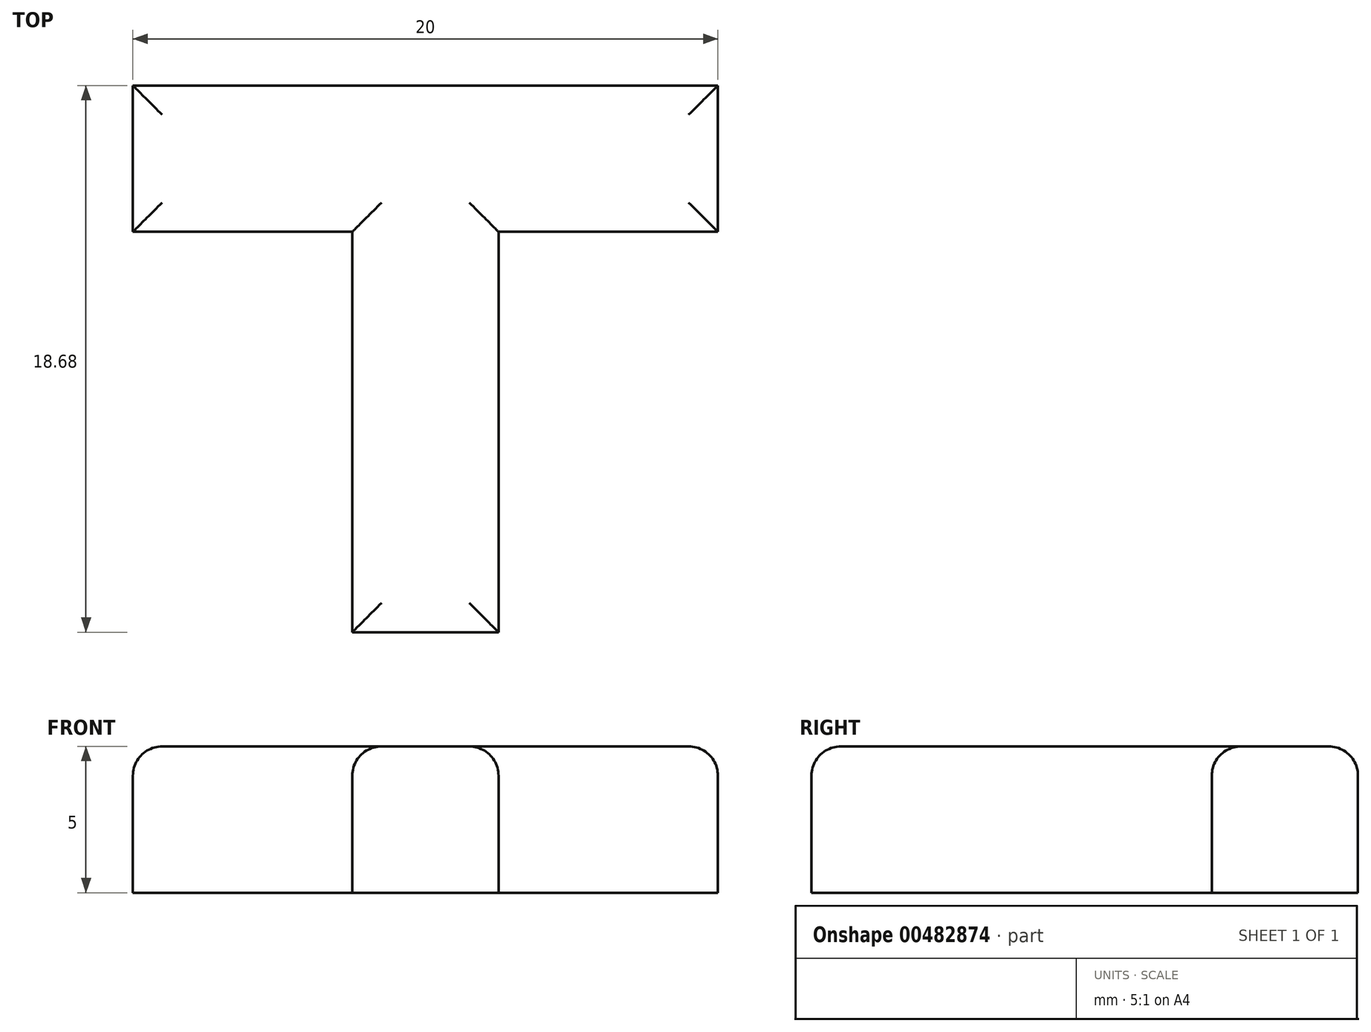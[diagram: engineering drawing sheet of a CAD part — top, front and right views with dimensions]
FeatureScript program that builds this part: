
annotation { "Feature Type Name" : "Feature", "Feature Type Description" : "" }
export const myFeature = defineFeature(function(context is Context, id is Id, definition is map)
    precondition{}
    {
        {
            var Q0;
            Q0=qCreatedBy(makeId("Top.planeOp"),FACE);
            var sketch = newSketch(context, id + "F0", { "sketchPlane" : qUnion([Q0])});
            skLineSegment(sketch, "E0", {"start": v(0, 0) * mm, "end": v(0, 13.68) * mm});
            skLineSegment(sketch, "E1", {"start": v(0, 13.68) * mm, "end": v(-7.5, 13.68) * mm});
            skLineSegment(sketch, "E2", {"start": v(-7.5, 13.68) * mm, "end": v(-7.5, 18.68) * mm});
            skLineSegment(sketch, "E3", {"start": v(-7.5, 18.68) * mm, "end": v(12.5, 18.68) * mm});
            skLineSegment(sketch, "E4", {"start": v(12.5, 18.68) * mm, "end": v(12.5, 13.68) * mm});
            skLineSegment(sketch, "E5", {"start": v(12.5, 13.68) * mm, "end": v(5, 13.68) * mm});
            skLineSegment(sketch, "E6", {"start": v(5, 13.68) * mm, "end": v(5, 0) * mm});
            skLineSegment(sketch, "E7", {"start": v(5, 0) * mm, "end": v(0, 0) * mm});
            skSolve(sketch);
        }
        {
            var Q0;
            Q0 = qSketchRegion(id + "F0", true);
            extrude(context, id + "F1", {"entities" : qUnion([Q0]), "depth" : 5 * mm});
        }
        {
            var Q0;
            Q0=makeQuery(id+"F1.opExtrude","CAP_EDGE",EDGE,{"disambiguationData":[OSD([sQuery(id+"F0.wireOp",EDGE,"E0")])],"isStart":false});
            var Q1;
            Q1=makeQuery(id+"F1.opExtrude","CAP_EDGE",EDGE,{"disambiguationData":[OSD([sQuery(id+"F0.wireOp",EDGE,"E7")])],"isStart":false});
            var Q2;
            Q2=makeQuery(id+"F1.opExtrude","CAP_EDGE",EDGE,{"disambiguationData":[OSD([sQuery(id+"F0.wireOp",EDGE,"E6")])],"isStart":false});
            var Q3;
            Q3=makeQuery(id+"F1.opExtrude","CAP_EDGE",EDGE,{"disambiguationData":[OSD([sQuery(id+"F0.wireOp",EDGE,"E5")])],"isStart":false});
            var Q4;
            Q4=makeQuery(id+"F1.opExtrude","CAP_EDGE",EDGE,{"disambiguationData":[OSD([sQuery(id+"F0.wireOp",EDGE,"E4")])],"isStart":false});
            var Q5;
            Q5=makeQuery(id+"F1.opExtrude","CAP_EDGE",EDGE,{"disambiguationData":[OSD([sQuery(id+"F0.wireOp",EDGE,"E3")])],"isStart":false});
            var Q6;
            Q6=makeQuery(id+"F1.opExtrude","CAP_EDGE",EDGE,{"disambiguationData":[OSD([sQuery(id+"F0.wireOp",EDGE,"E2")])],"isStart":false});
            var Q7;
            Q7=makeQuery(id+"F1.opExtrude","CAP_EDGE",EDGE,{"disambiguationData":[OSD([sQuery(id+"F0.wireOp",EDGE,"E1")])],"isStart":false});
            fillet(context, id + "F2", {"entities" : qUnion([Q0, Q1, Q2, Q3, Q4, Q5, Q6, Q7]), "radius" : 1 * mm, "tangentPropagation" : true, "allowEdgeOverflow" : false});
        }
    });
